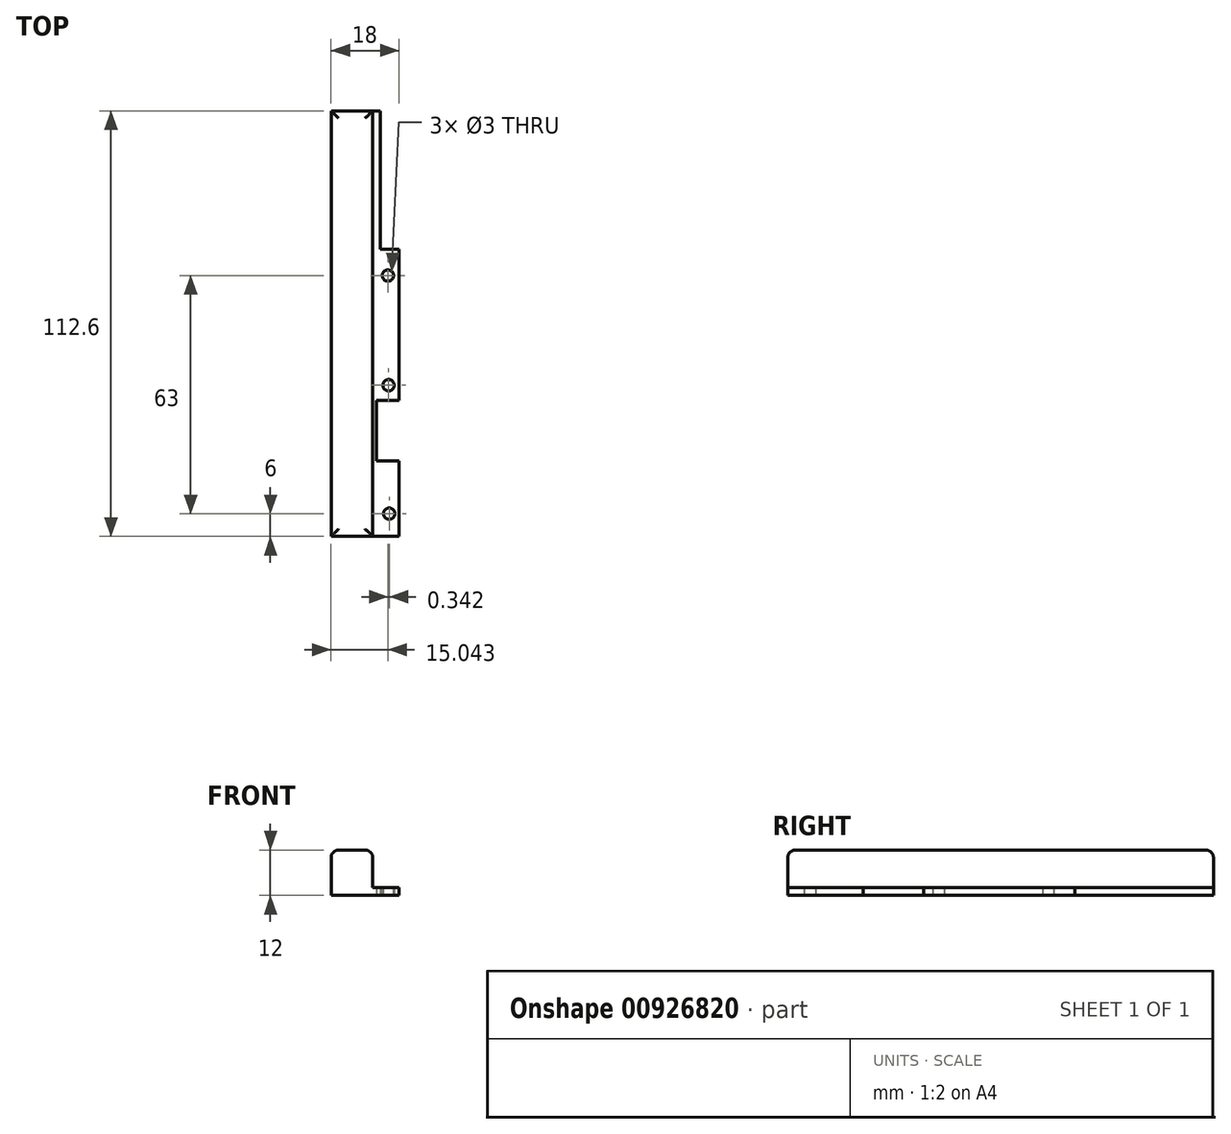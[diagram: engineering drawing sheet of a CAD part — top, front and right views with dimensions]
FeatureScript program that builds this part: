
annotation { "Feature Type Name" : "Feature", "Feature Type Description" : "" }
export const myFeature = defineFeature(function(context is Context, id is Id, definition is map)
    precondition{}
    {
        {
            var Q0;
            Q0=qCreatedBy(makeId("Top.planeOp"),FACE);
            var sketch = newSketch(context, id + "F0", { "sketchPlane" : qUnion([Q0])});
            skLineSegment(sketch, "E0", {"start": v(-31.77, 43.24) * mm, "end": v(-31.77, 6.64) * mm});
            skLineSegment(sketch, "E1", {"start": v(-31.77, 6.64) * mm, "end": v(-26.77, 6.64) * mm});
            skLineSegment(sketch, "E2", {"start": v(-26.77, 6.64) * mm, "end": v(-26.77, -33.36) * mm});
            skLineSegment(sketch, "E3", {"start": v(-26.77, -33.36) * mm, "end": v(-32.77, -33.36) * mm});
            skLineSegment(sketch, "E4", {"start": v(-32.77, -33.36) * mm, "end": v(-32.77, -49.36) * mm});
            skLineSegment(sketch, "E5", {"start": v(-32.77, -49.36) * mm, "end": v(-26.77, -49.36) * mm});
            skLineSegment(sketch, "E6", {"start": v(-26.77, -49.36) * mm, "end": v(-26.77, -69.36) * mm});
            skLineSegment(sketch, "E7", {"start": v(-26.77, -69.36) * mm, "end": v(-44.77, -69.36) * mm});
            skLineSegment(sketch, "E8", {"start": v(-44.77, -69.36) * mm, "end": v(-44.77, 43.24) * mm});
            skLineSegment(sketch, "E9", {"start": v(-44.77, 43.24) * mm, "end": v(-31.77, 43.24) * mm});
            skLineSegment(sketch, "E10", {"start": v(-32.77, -41.36) * mm, "end": v(-33.77, -41.36) * mm, "construction": true});
            skLineSegment(sketch, "E11", {"start": v(-33.77, -69.36) * mm, "end": v(-33.77, 43.24) * mm});
            skSolve(sketch);
        }
        {
            var Q0;
            Q0 = qSketchRegion(id + "F0", true);
            extrude(context, id + "F1", {"entities" : qUnion([Q0]), "depth" : 2 * mm, "offsetDistance" : 25 * mm});
        }
        {
            var Q0;
            Q0=makeQuery(id+"F1.opExtrude","CAP_FACE",FACE,{"disambiguationData":[OSD([sQuery(id+"F0.wireOp",EDGE,"E0"),sQuery(id+"F0.wireOp",EDGE,"E1"),sQuery(id+"F0.wireOp",EDGE,"E2"),sQuery(id+"F0.wireOp",EDGE,"E3"),sQuery(id+"F0.wireOp",EDGE,"E4"),sQuery(id+"F0.wireOp",EDGE,"E5"),sQuery(id+"F0.wireOp",EDGE,"E6"),sQuery(id+"F0.wireOp",EDGE,"E7"),sQuery(id+"F0.wireOp",EDGE,"E8"),sQuery(id+"F0.wireOp",EDGE,"E9")])],"isStart":false});
            cPlane(context, id + "F2", {"entities" : qUnion([Q0]), "cplaneType" : CPlaneType.OFFSET, "offset" : 0 * mm, "width" : 150 * mm, "height" : 150 * mm});
        }
        {
            var Q0;
            Q0=qCreatedBy(id+"F2.planeOp",FACE);
            var sketch = newSketch(context, id + "F3", { "sketchPlane" : qUnion([Q0])});
            skLineSegment(sketch, "E12.0", {"start": v(-44.77, -69.36) * mm, "end": v(-44.77, 43.24) * mm});
            skLineSegment(sketch, "E13.0", {"start": v(-33.77, -69.36) * mm, "end": v(-33.77, 43.24) * mm});
            skLineSegment(sketch, "E14", {"start": v(-44.77, 43.24) * mm, "end": v(-33.77, 43.24) * mm});
            skLineSegment(sketch, "E15", {"start": v(-44.77, -69.36) * mm, "end": v(-33.77, -69.36) * mm});
            skSolve(sketch);
        }
        {
            var Q0;
            Q0 = qSketchRegion(id + "F3", true);
            extrude(context, id + "F4", {"entities" : qUnion([Q0]), "operationType" : NewBodyOperationType.ADD, "depth" : 10 * mm, "offsetDistance" : 25 * mm});
        }
        {
            var Q0;
            Q0=makeQuery(id+"F4.opExtrude","CAP_EDGE",EDGE,{"disambiguationData":[OSD([sQuery(id+"F3.wireOp",EDGE,"E14")])],"isStart":false});
            var Q1;
            Q1=makeQuery(id+"F4.opExtrude","CAP_EDGE",EDGE,{"disambiguationData":[OSD([sQuery(id+"F3.wireOp",EDGE,"E12.0")])],"isStart":false});
            var Q2;
            Q2=makeQuery(id+"F4.opExtrude","CAP_EDGE",EDGE,{"disambiguationData":[OSD([sQuery(id+"F3.wireOp",EDGE,"E13.0")])],"isStart":false});
            var Q3;
            Q3=makeQuery(id+"F4.opExtrude","CAP_EDGE",EDGE,{"disambiguationData":[OSD([sQuery(id+"F3.wireOp",EDGE,"E15")])],"isStart":false});
            fillet(context, id + "F5", {"entities" : qUnion([Q0, Q1, Q2, Q3]), "radius" : 2 * mm, "tangentPropagation" : true, "allowEdgeOverflow" : false});
        }
        {
            var Q0;
            Q0=makeQuery(id+"F1.opExtrude","CAP_FACE",FACE,{"disambiguationData":[OSD([sQuery(id+"F0.wireOp",EDGE,"E0"),sQuery(id+"F0.wireOp",EDGE,"E1"),sQuery(id+"F0.wireOp",EDGE,"E2"),sQuery(id+"F0.wireOp",EDGE,"E3"),sQuery(id+"F0.wireOp",EDGE,"E4"),sQuery(id+"F0.wireOp",EDGE,"E5"),sQuery(id+"F0.wireOp",EDGE,"E6"),sQuery(id+"F0.wireOp",EDGE,"E7"),sQuery(id+"F0.wireOp",EDGE,"E8"),sQuery(id+"F0.wireOp",EDGE,"E9")])],"isStart":false});
            var sketch = newSketch(context, id + "F6", { "sketchPlane" : qUnion([Q0])});
            skLineSegment(sketch, "E16", {"start": v(-29.27, 6.64) * mm, "end": v(-29.27, -0.36) * mm, "construction": true});
            skLineSegment(sketch, "E17", {"start": v(-29.77, -33.36) * mm, "end": v(-29.77, -29.36) * mm, "construction": true});
            skLineSegment(sketch, "E18", {"start": v(-30.27, -69.36) * mm, "end": v(-30.27, -63.36) * mm, "construction": true});
            skLineSegment(sketch, "E19", {"start": v(-26.77, -10.6) * mm, "end": v(-29.77, -10.6) * mm, "construction": true});
            skLineSegment(sketch, "E20", {"start": v(-29.77, 6.64) * mm, "end": v(-29.27, -85.38) * mm, "construction": true});
            skCircle(sketch, "E21", {"center": v(-29.73, -0.36) * mm, "radius": 1.5 * mm});
            skCircle(sketch, "E22", {"center": v(-29.57, -29.36) * mm, "radius": 1.5 * mm});
            skCircle(sketch, "E23", {"center": v(-29.38, -63.36) * mm, "radius": 1.5 * mm});
            skSolve(sketch);
        }
        {
            var Q0;
            Q0=makeQuery(id+"F6.imprint","IMPRINT",FACE,{"disambiguationData":[TD([[makeQuery(id+"F6.imprint","IMPRINT",EDGE,{"derivedFrom":sQuery(id+"F6.wireOp",EDGE,"E21")}),1.0]])]});
            var Q1;
            Q1=makeQuery(id+"F6.imprint","IMPRINT",FACE,{"disambiguationData":[TD([[makeQuery(id+"F6.imprint","IMPRINT",EDGE,{"derivedFrom":sQuery(id+"F6.wireOp",EDGE,"E22")}),1.0]])]});
            var Q2;
            Q2=makeQuery(id+"F6.imprint","IMPRINT",FACE,{"disambiguationData":[TD([[makeQuery(id+"F6.imprint","IMPRINT",EDGE,{"derivedFrom":sQuery(id+"F6.wireOp",EDGE,"E23")}),1.0]])]});
            extrude(context, id + "F7", {"entities" : qUnion([Q0, Q1, Q2]), "operationType" : NewBodyOperationType.REMOVE, "oppositeDirection" : true, "depth" : 25 * mm, "offsetDistance" : 25 * mm});
        }
    });
